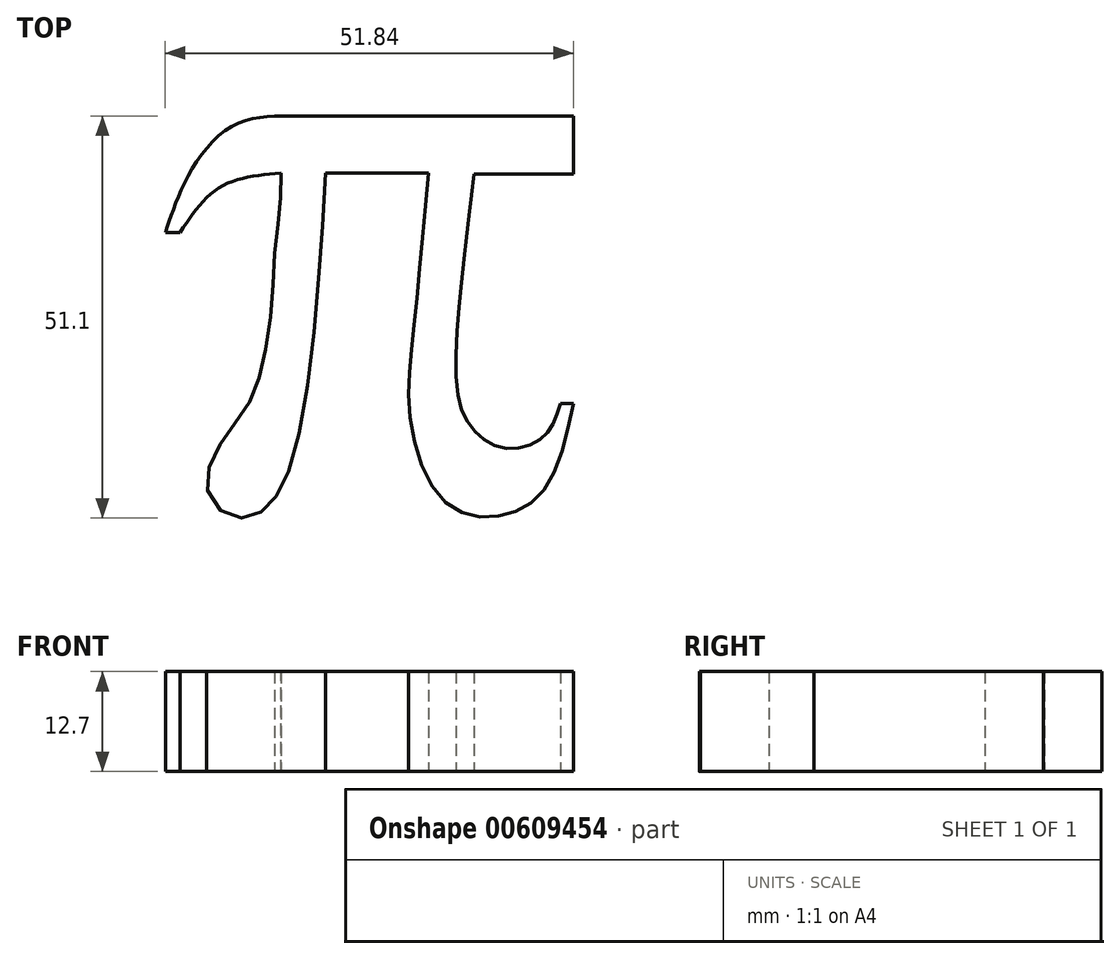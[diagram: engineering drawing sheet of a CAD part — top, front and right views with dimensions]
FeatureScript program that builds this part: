
annotation { "Feature Type Name" : "Feature", "Feature Type Description" : "" }
export const myFeature = defineFeature(function(context is Context, id is Id, definition is map)
    precondition{}
    {
        {
            var Q0;
            Q0=qCreatedBy(makeId("Top.planeOp"),FACE);
            var sketch = newSketch(context, id + "F0", { "sketchPlane" : qUnion([Q0])});
            skLineSegment(sketch, "E0", {"start": v(24.76, 27.11) * mm, "end": v(-13.18, 27.11) * mm});
            skLineSegment(sketch, "E1", {"start": v(-6.72, 19.82) * mm, "end": v(6.35, 19.82) * mm});
            skLineSegment(sketch, "E2", {"start": v(12.15, 19.7) * mm, "end": v(24.76, 19.7) * mm});
            skLineSegment(sketch, "E3", {"start": v(24.76, 19.7) * mm, "end": v(24.76, 27.11) * mm});
            skFitSpline(sketch, "E4", {"points": [v(-6.72, 19.82) * mm, v(-8.17, 0) * mm, v(-10.94, -16.6) * mm, v(-13.45, -21.88) * mm, v(-15.82, -23.69) * mm, v(-19, -23.69) * mm, v(-21.63, -20.82) * mm, v(-21.37, -17.12) * mm, v(-19, -12.9) * mm, v(-16.35, -9.2) * mm, v(-14.77, -4.46) * mm, v(-13.58, 2.67) * mm, v(-13.18, 9.8) * mm, v(-12.52, 15.47) * mm, v(-12.4, 19.82) * mm], "startDerivative": vector(-8.84, -153.47) * mm, "endDerivative": vector(-0.09, 70.67) * mm});
            skFitSpline(sketch, "E5", {"points": [v(-12.4, 19.82) * mm, v(-20.05, 18.1) * mm, v(-25.2, 12.3) * mm], "startDerivative": vector(-16.5, -1.36) * mm, "endDerivative": vector(-9.09, -13.7) * mm});
            skFitSpline(sketch, "E6", {"points": [v(-25.2, 12.3) * mm, v(-27.08, 12.3) * mm], "startDerivative": vector(-1.89, 0) * mm, "endDerivative": vector(-1.89, 0) * mm});
            skFitSpline(sketch, "E7", {"points": [v(-13.18, 27.11) * mm, v(-18.46, 25.9) * mm, v(-23.21, 21.14) * mm, v(-25.82, 15.86) * mm, v(-27.08, 12.3) * mm], "startDerivative": vector(-21.68, -2.06) * mm, "endDerivative": vector(-5.44, -16.23) * mm});
            skFitSpline(sketch, "E8", {"points": [v(6.35, 19.82) * mm, v(4.46, 0) * mm, v(4.05, -11.46) * mm, v(8.53, -22.04) * mm, v(15.45, -23.69) * mm, v(21.15, -20.21) * mm, v(24.76, -9.42) * mm], "startDerivative": vector(-8.5, -95.15) * mm, "endDerivative": vector(15.44, 72.43) * mm});
            skFitSpline(sketch, "E9", {"points": [v(24.76, -9.42) * mm, v(23.1, -9.42) * mm], "startDerivative": vector(-1.65, 0) * mm, "endDerivative": vector(-1.65, 0) * mm});
            skFitSpline(sketch, "E10", {"points": [v(23.1, -9.42) * mm, v(21.94, -12.46) * mm, v(19.62, -14.52) * mm, v(15.69, -15.05) * mm, v(12.15, -12.86) * mm, v(10.06, -8.17) * mm, v(10.59, 6.38) * mm, v(12.15, 19.7) * mm], "startDerivative": vector(-8.8, -30.94) * mm, "endDerivative": vector(7.42, 59.83) * mm});
            skSolve(sketch);
        }
        {
            var Q0;
            Q0=makeQuery(id+"F0.imprint","IMPRINT",FACE,{"disambiguationData":[TD([[makeQuery(id+"F0.imprint","IMPRINT",EDGE,{"derivedFrom":sQuery(id+"F0.wireOp",EDGE,"E0")}),1.0]])]});
            extrude(context, id + "F1", {"entities" : qUnion([Q0]), "depth" : 12.7 * mm, "offsetDistance" : 25.4 * mm});
        }
    });
